# Revit family: Kemper - 6500624000
name_source: partatom
category: Rohrzubehör
units: mm (PartAtom-declared; Revit-internal decimal feet)

## family parameters
Arbeitsebenenbasiert = Nein
Beim Laden mit Abzugskörper schneiden = Nein
Bemaßung runder Anschluss = Durchmesser verwenden
Gemeinsam genutzt = Nein
Immer vertikal = Ja
OmniClass-Nummer = 23.65.55.14
OmniClass-Titel = Valves for Liquid Services
Teiletyp = Ventil - Zerlegung in

## types (1)
- DN 40
    AssetType = Fixed
    Datanorm = 6500624000
    DurationUnit = Years
    Flow = 0
    Generation ID = Kemper - 6500624000
    Manufacturer = Kemper
    Material = gunmetal
    Model = 650 06, KHS Flow-Splitter unit - dynamic, FPT
    Modelnumber = 6500624000
    Shape = Valve
    Size DN = 40
    Tmax, Control °C = 0
    Tmin, Control °C = 0
    WarrantyDurationUnit = Years
    collision height = 234 mm
    collision length = 206 mm  [stored 0.675853 ft]
    collision volume = 206 x 88.267025 x 234.017025
    collision width = 88 mm
    design = pass
    kVs-Value = 0
    max. differential pressure = 0
    perm. operating Temperature °C = 90
    perm. operating pressure Bar = 16
    productgroup = KEMPER Hygiene System
    sound insulation class = 1
    type = Sicherungsarmatur
    type of connection = Flow-Splitter main pass with female thread, female-thread outlets
    typedescription = KEMPER Hygiene System, 650 06, KHS Flow-Splitter unit - dynamic, FPT
    valvetype = Ringleitungsarmatur

note: [stored X ft] marks values corroborated as IEEE doubles in the binary element streams (Revit-internal decimal feet)
